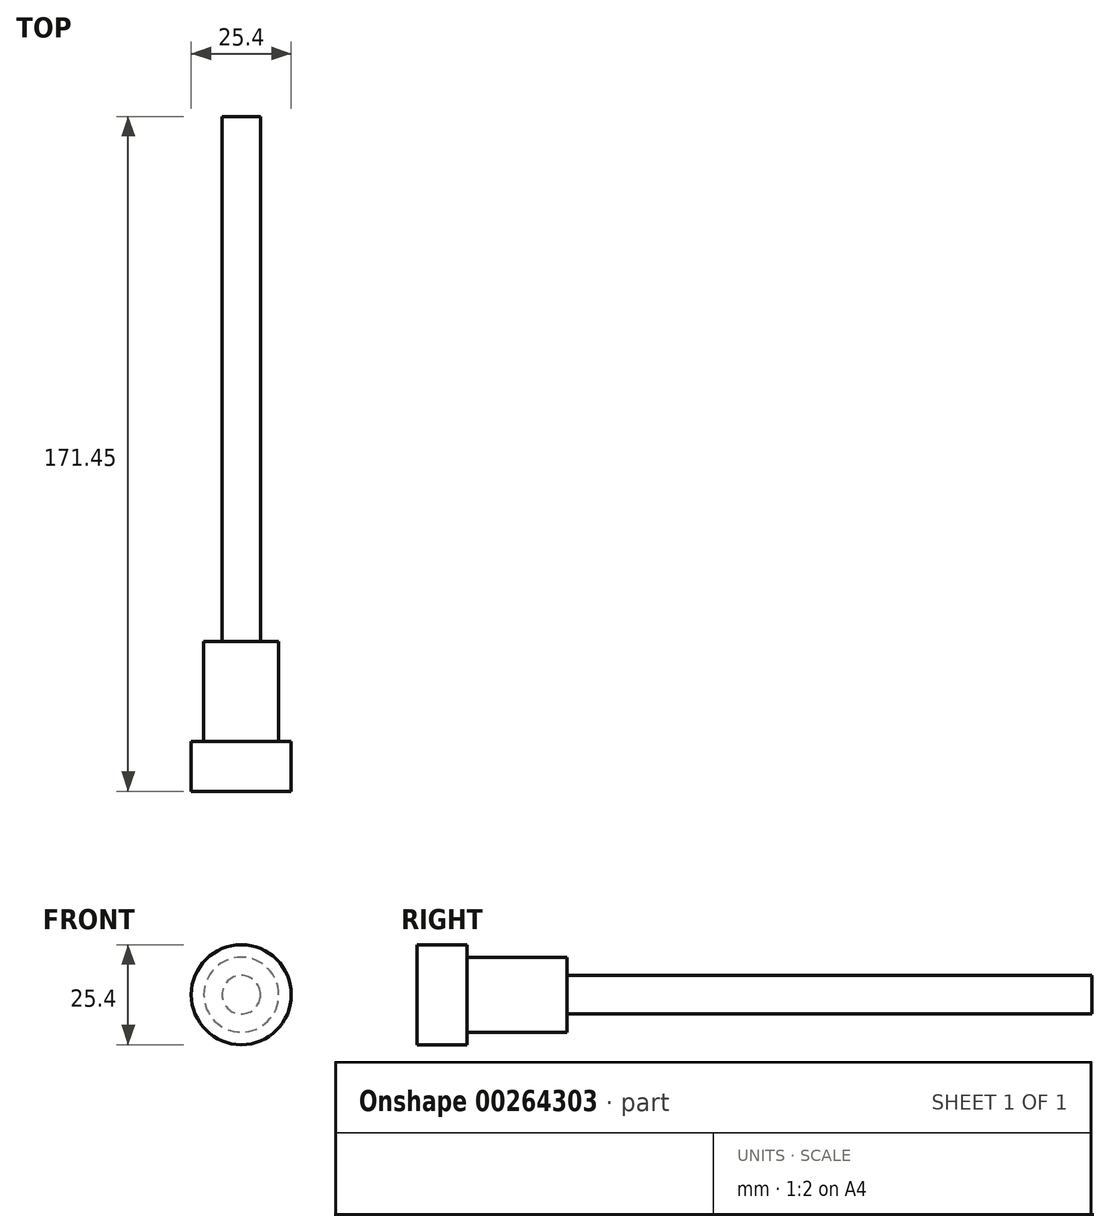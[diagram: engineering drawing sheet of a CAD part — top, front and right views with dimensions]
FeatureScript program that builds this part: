
annotation { "Feature Type Name" : "Feature", "Feature Type Description" : "" }
export const myFeature = defineFeature(function(context is Context, id is Id, definition is map)
    precondition{}
    {
        {
            var Q0;
            Q0=qCreatedBy(makeId("Front.planeOp"),FACE);
            var sketch = newSketch(context, id + "F0", { "sketchPlane" : qUnion([Q0])});
            skCircle(sketch, "E0", {"center": v(0, 0) * mm, "radius": 4.9 * mm});
            skSolve(sketch);
        }
        {
            var Q0;
            Q0=makeQuery(id+"F0.imprint","IMPRINT",FACE,{"disambiguationData":[TD([[makeQuery(id+"F0.imprint","IMPRINT",EDGE,{"derivedFrom":sQuery(id+"F0.wireOp",EDGE,"E0")}),1.0]])]});
            extrude(context, id + "F1", {"entities" : qUnion([Q0]), "oppositeDirection" : true, "depth" : 133.35 * mm});
        }
        {
            var Q0;
            Q0=qCreatedBy(makeId("Front.planeOp"),FACE);
            var sketch = newSketch(context, id + "F2", { "sketchPlane" : qUnion([Q0])});
            skCircle(sketch, "E1", {"center": v(0, 0) * mm, "radius": 9.53 * mm});
            skSolve(sketch);
        }
        {
            var Q0;
            Q0=makeQuery(id+"F2.imprint","IMPRINT",FACE,{"disambiguationData":[TD([[makeQuery(id+"F2.imprint","IMPRINT",EDGE,{"derivedFrom":sQuery(id+"F2.wireOp",EDGE,"E1")}),1.0]])]});
            extrude(context, id + "F3", {"entities" : qUnion([Q0]), "operationType" : NewBodyOperationType.ADD, "depth" : 25.4 * mm});
        }
        {
            var Q0;
            Q0=makeQuery(id+"F3.opExtrude","CAP_FACE",FACE,{"disambiguationData":[OSD([sQuery(id+"F2.wireOp",EDGE,"E1")])],"isStart":false});
            var sketch = newSketch(context, id + "F4", { "sketchPlane" : qUnion([Q0])});
            skCircle(sketch, "E2", {"center": v(0, 0) * mm, "radius": 12.7 * mm});
            skSolve(sketch);
        }
        {
            var Q0;
            Q0 = qSketchRegion(id + "F4", true);
            extrude(context, id + "F5", {"entities" : qUnion([Q0]), "operationType" : NewBodyOperationType.ADD, "depth" : 12.7 * mm});
        }
    });
